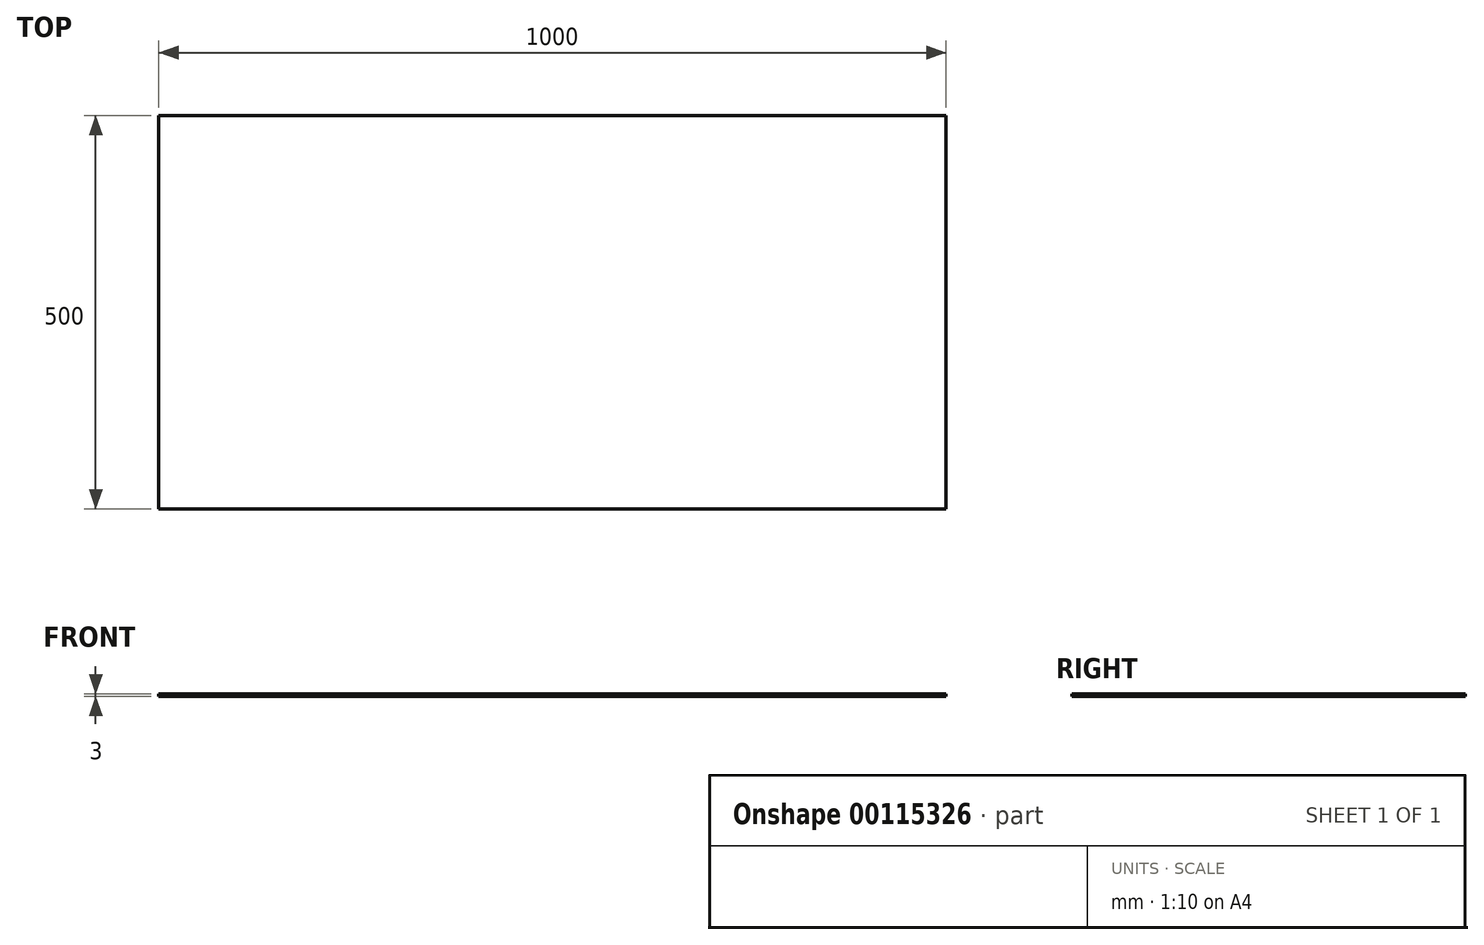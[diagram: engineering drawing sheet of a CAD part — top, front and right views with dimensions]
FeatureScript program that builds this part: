
annotation { "Feature Type Name" : "Feature", "Feature Type Description" : "" }
export const myFeature = defineFeature(function(context is Context, id is Id, definition is map)
    precondition{}
    {
        {
            var Q0;
            Q0=qCreatedBy(makeId("Top.planeOp"),FACE);
            var sketch = newSketch(context, id + "F0", { "sketchPlane" : qUnion([Q0])});
            skLineSegment(sketch, "E0.bottom", {"start": v(0, 0) * mm, "end": v(1000, 0) * mm});
            skLineSegment(sketch, "E0.top", {"start": v(0, 500) * mm, "end": v(1000, 500) * mm});
            skLineSegment(sketch, "E0.left", {"start": v(0, 0) * mm, "end": v(0, 500) * mm});
            skLineSegment(sketch, "E0.right", {"start": v(1000, 0) * mm, "end": v(1000, 500) * mm});
            skSolve(sketch);
        }
        {
            var Q0;
            Q0 = qSketchRegion(id + "F0", true);
            extrude(context, id + "F1", {"entities" : qUnion([Q0]), "depth" : 3 * mm});
        }
    });
